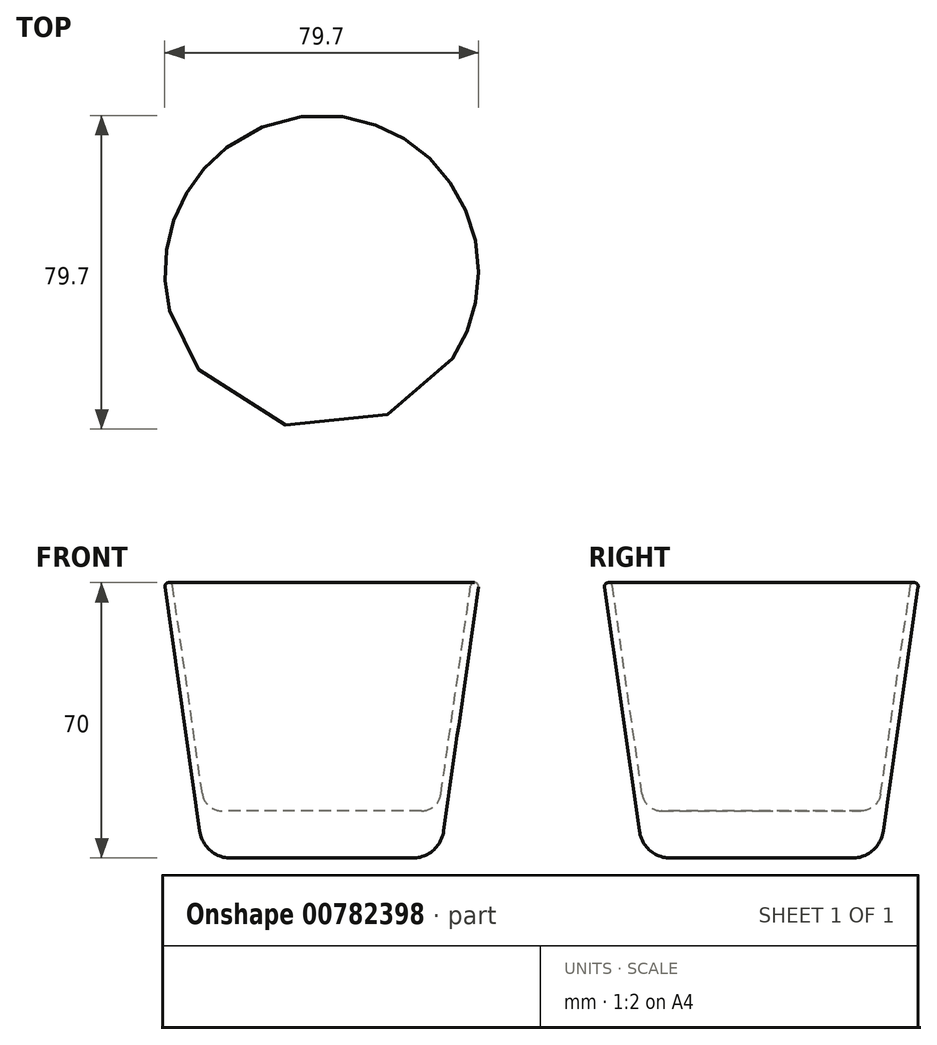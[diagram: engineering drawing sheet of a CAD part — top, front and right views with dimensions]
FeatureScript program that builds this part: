
annotation { "Feature Type Name" : "Feature", "Feature Type Description" : "" }
export const myFeature = defineFeature(function(context is Context, id is Id, definition is map)
    precondition{}
    {
        {
            var Q0;
            Q0=qCreatedBy(makeId("Front.planeOp"),FACE);
            var sketch = newSketch(context, id + "F0", { "sketchPlane" : qUnion([Q0])});
            skLineSegment(sketch, "E0", {"start": v(0, 0) * mm, "end": v(0, 78.3) * mm, "construction": true});
            skLineSegment(sketch, "E1", {"start": v(0, 0) * mm, "end": v(23.06, 0) * mm});
            skLineSegment(sketch, "E2", {"start": v(30.98, 6.87) * mm, "end": v(39.84, 68.86) * mm});
            skPoint(sketch, "E3.visualSharp", {"position": v(30, 0) * mm});
            skArc(sketch, "E3.filletArc", {"start": v(23.06, 0) * mm, "mid": v(28.3, 1.96) * mm, "end": v(30.98, 6.87) * mm});
            skLineSegment(sketch, "E4.0", {"start": v(30.3, 16.3) * mm, "end": v(37.86, 69.14) * mm});
            skLineSegment(sketch, "E5.0", {"start": v(0, 12) * mm, "end": v(25.36, 12) * mm});
            skArc(sketch, "E6.filletArc", {"start": v(25.36, 12) * mm, "mid": v(28.63, 13.22) * mm, "end": v(30.3, 16.3) * mm});
            skArc(sketch, "E7", {"start": v(39.84, 68.86) * mm, "mid": v(38.99, 69.99) * mm, "end": v(37.86, 69.14) * mm});
            skPoint(sketch, "E7.first.point", {"position": v(37.86, 69.14) * mm});
            skPoint(sketch, "E7.second.point", {"position": v(38.85, 70) * mm});
            skPoint(sketch, "E7.third.point", {"position": v(39.84, 68.86) * mm});
            skPoint(sketch, "E8.orphan", {"position": v(40, 70) * mm});
            skLineSegment(sketch, "E9", {"start": v(0, 12) * mm, "end": v(0, 0) * mm});
            skSolve(sketch);
        }
        {
            var Q0;
            Q0=makeQuery(id+"F0.imprint","IMPRINT",FACE,{"disambiguationData":[TD([[makeQuery(id+"F0.imprint","IMPRINT",EDGE,{"derivedFrom":sQuery(id+"F0.wireOp",EDGE,"E1")}),1.0]])]});
            var Q1;
            Q1=sQuery(id+"F0.wireOp",EDGE,"E9");
            revolve(context, id + "F1", {"surfaceOperationType" : NewSurfaceOperationType.NEW, "entities" : qUnion([Q0]), "axis" : qUnion([Q1]), "revolveType" : RevolveType.FULL});
        }
    });
